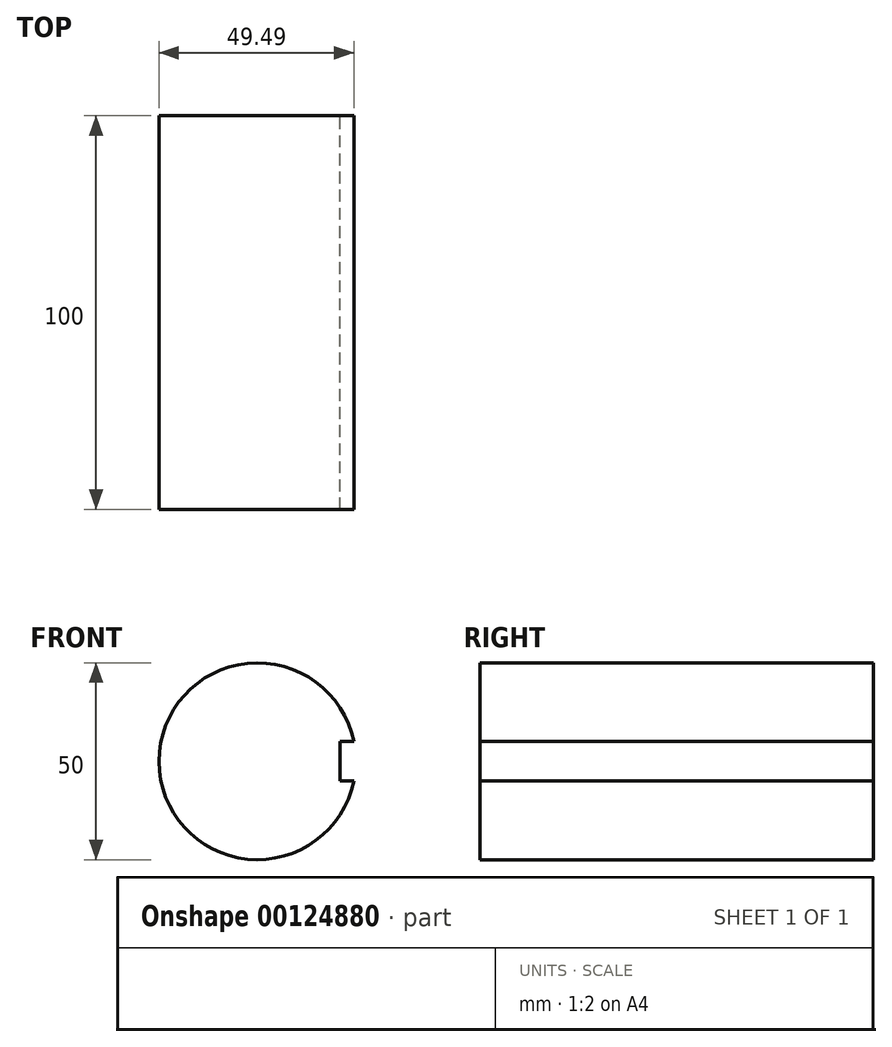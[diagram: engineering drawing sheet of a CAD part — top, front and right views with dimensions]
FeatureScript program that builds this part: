
annotation { "Feature Type Name" : "Feature", "Feature Type Description" : "" }
export const myFeature = defineFeature(function(context is Context, id is Id, definition is map)
    precondition{}
    {
        {
            var Q0;
            Q0=qCreatedBy(makeId("Front.planeOp"),FACE);
            var sketch = newSketch(context, id + "F0", { "sketchPlane" : qUnion([Q0])});
            skCircle(sketch, "E0", {"center": v(0, 0) * mm, "radius": 25 * mm});
            skSolve(sketch);
        }
        {
            var Q0;
            Q0=makeQuery(id+"F0.imprint","IMPRINT",FACE,{"disambiguationData":[TD([[makeQuery(id+"F0.imprint","IMPRINT",EDGE,{"derivedFrom":sQuery(id+"F0.wireOp",EDGE,"E0")}),1.0]])]});
            extrude(context, id + "F1", {"entities" : qUnion([Q0]), "depth" : 100 * mm});
        }
        {
            var Q0;
            Q0=qCreatedBy(makeId("Front.planeOp"),FACE);
            var sketch = newSketch(context, id + "F2", { "sketchPlane" : qUnion([Q0])});
            skCircle(sketch, "E1.0", {"center": v(0, 0) * mm, "radius": 25 * mm, "construction": true});
            skLineSegment(sketch, "E2.bottom", {"start": v(29, -5) * mm, "end": v(21, -5) * mm});
            skLineSegment(sketch, "E2.top", {"start": v(29, 5) * mm, "end": v(21, 5) * mm});
            skLineSegment(sketch, "E2.left", {"start": v(29, -5) * mm, "end": v(29, 5) * mm});
            skLineSegment(sketch, "E2.right", {"start": v(21, -5) * mm, "end": v(21, 5) * mm});
            skPoint(sketch, "E2.middle", {"position": v(25, 0) * mm});
            skSolve(sketch);
        }
        {
            var Q0;
            Q0=makeQuery(id+"F2.imprint","IMPRINT",FACE,{"disambiguationData":[TD([[makeQuery(id+"F2.imprint","IMPRINT",EDGE,{"derivedFrom":sQuery(id+"F2.wireOp",EDGE,"E2.bottom")}),-1.0]])]});
            extrude(context, id + "F3", {"entities" : qUnion([Q0]), "operationType" : NewBodyOperationType.REMOVE, "endBound" : BoundingType.THROUGH_ALL, "depth" : 25 * mm});
        }
    });
